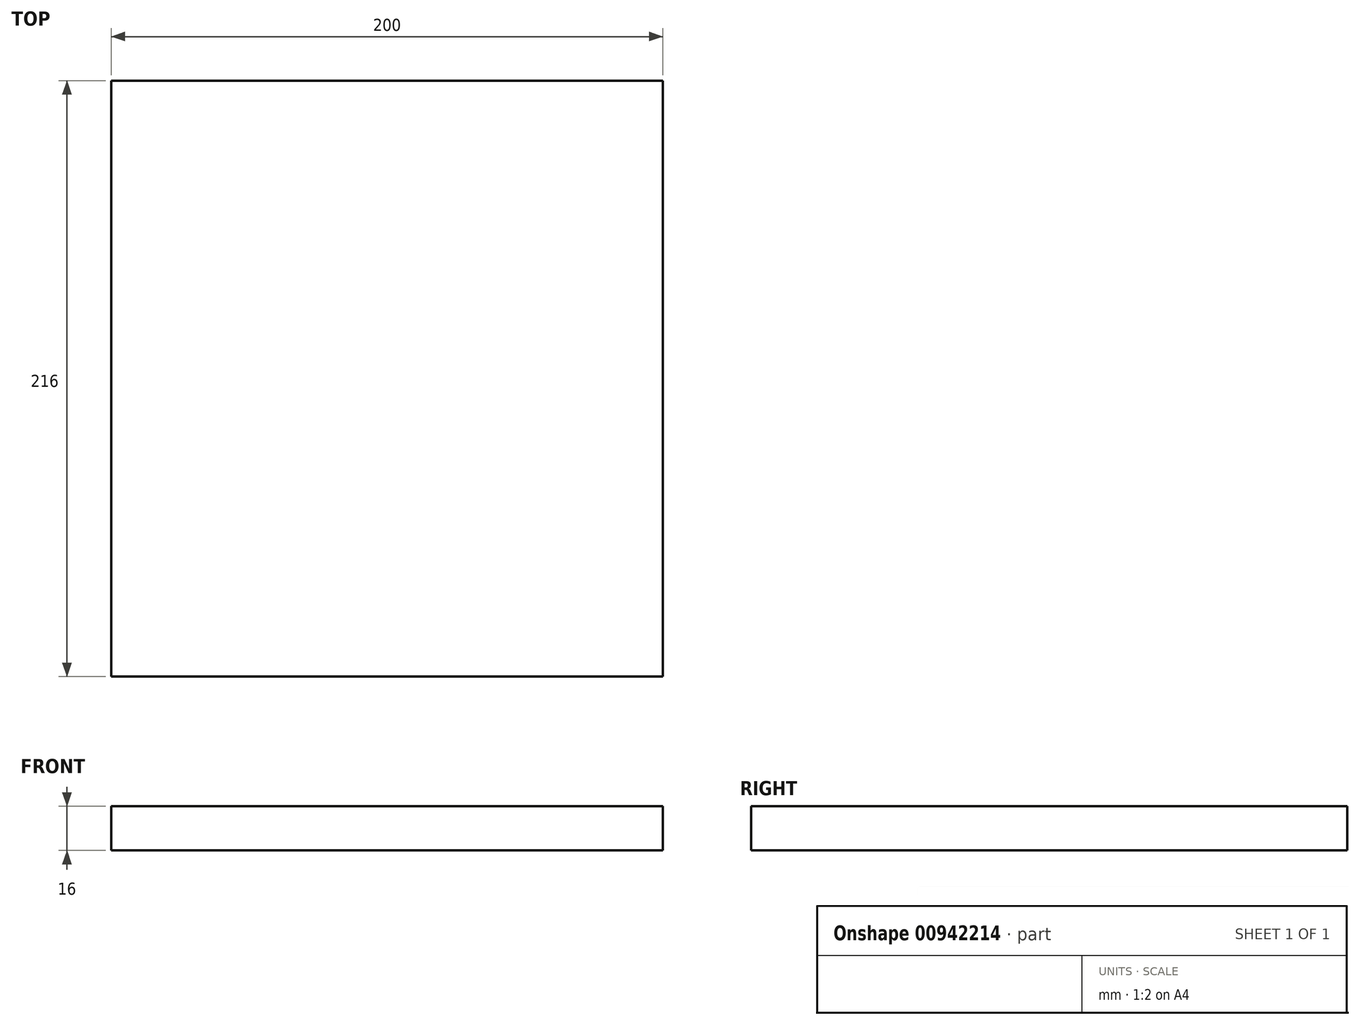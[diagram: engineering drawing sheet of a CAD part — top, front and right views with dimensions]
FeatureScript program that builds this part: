
annotation { "Feature Type Name" : "Feature", "Feature Type Description" : "" }
export const myFeature = defineFeature(function(context is Context, id is Id, definition is map)
    precondition{}
    {
        {
            var Q0;
            Q0=qCreatedBy(makeId("Top.planeOp"),FACE);
            var sketch = newSketch(context, id + "F0", { "sketchPlane" : qUnion([Q0])});
            skLineSegment(sketch, "E0", {"start": v(-71.17, -56.32) * mm, "end": v(-111.07, -56.32) * mm});
            skLineSegment(sketch, "E1.bottom", {"start": v(-111.07, -56.32) * mm, "end": v(88.93, -56.32) * mm});
            skLineSegment(sketch, "E1.top", {"start": v(-111.07, 143.68) * mm, "end": v(88.93, 143.68) * mm});
            skLineSegment(sketch, "E1.left", {"start": v(-111.07, -56.32) * mm, "end": v(-111.07, 143.68) * mm});
            skLineSegment(sketch, "E1.right", {"start": v(88.93, -56.32) * mm, "end": v(88.93, 143.68) * mm});
            skSolve(sketch);
        }
        {
            var Q0;
            Q0=makeQuery(id+"F0.imprint","IMPRINT",FACE,{"disambiguationData":[TD([[makeQuery(id+"F0.imprint","IMPRINT",EDGE,{"derivedFrom":sQuery(id+"F0.wireOp",EDGE,"E1.top")}),-1.0]])]});
            extrude(context, id + "F1", {"entities" : qUnion([Q0]), "depth" : 16 * mm, "offsetDistance" : 25 * mm});
        }
        {
            var Q0;
            Q0=makeQuery(id+"F1.opExtrude","SWEPT_FACE",FACE,{"disambiguationData":[OSD([sQuery(id+"F0.wireOp",EDGE,"E1.top")])]});
            var sketch = newSketch(context, id + "F2", { "sketchPlane" : qUnion([Q0])});
            skLineSegment(sketch, "E2.bottom", {"start": v(-88.93, 0) * mm, "end": v(111.07, 0) * mm});
            skLineSegment(sketch, "E2.top", {"start": v(-88.93, 200) * mm, "end": v(111.07, 200) * mm});
            skLineSegment(sketch, "E2.left", {"start": v(-88.93, 0) * mm, "end": v(-88.93, 200) * mm});
            skLineSegment(sketch, "E2.right", {"start": v(111.07, 0) * mm, "end": v(111.07, 200) * mm});
            skSolve(sketch);
        }
        {
            var Q0;
            {var subQ0=sQuery(id+"F2.wireOp",EDGE,"E2.bottom");Q0=makeQuery(id+"F2.imprint","IMPRINT",FACE,{"disambiguationData":[TD([[makeQuery(id+"F2.imprint","IMPRINT",EDGE,{"derivedFrom":subQ0}),-1.0]])]});}
            extrude(context, id + "F3", {"entities" : qUnion([Q0]), "operationType" : NewBodyOperationType.ADD, "depth" : 16 * mm, "offsetDistance" : 25 * mm});
        }
    });
